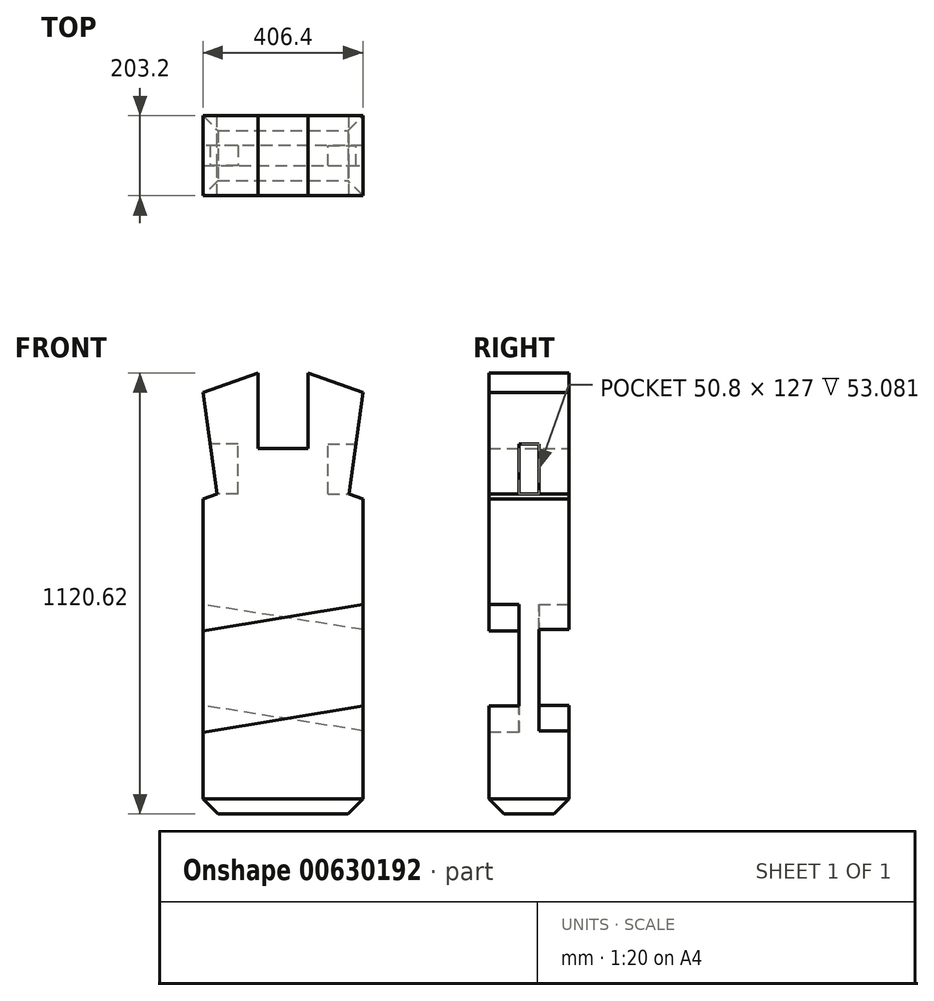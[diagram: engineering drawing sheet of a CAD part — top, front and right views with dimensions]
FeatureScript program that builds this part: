
annotation { "Feature Type Name" : "Feature", "Feature Type Description" : "" }
export const myFeature = defineFeature(function(context is Context, id is Id, definition is map)
    precondition{}
    {
        {
            var Q0;
            Q0=qCreatedBy(makeId("Front.planeOp"),FACE);
            var sketch = newSketch(context, id + "F0", { "sketchPlane" : qUnion([Q0])});
            skLineSegment(sketch, "E0.bottom", {"start": v(-203.2, 255.59) * mm, "end": v(203.2, 255.59) * mm});
            skLineSegment(sketch, "E0.top", {"start": v(-203.2, -255.59) * mm, "end": v(203.2, -255.59) * mm});
            skLineSegment(sketch, "E0.left", {"start": v(-203.2, 255.59) * mm, "end": v(-203.2, -255.59) * mm});
            skLineSegment(sketch, "E0.right", {"start": v(203.2, 255.59) * mm, "end": v(203.2, -255.59) * mm});
            skPoint(sketch, "E0.middle", {"position": v(0, 0) * mm});
            skLineSegment(sketch, "E1", {"start": v(-203.2, 255.59) * mm, "end": v(0, 329.25) * mm});
            skLineSegment(sketch, "E2", {"start": v(0, 329.25) * mm, "end": v(203.2, 255.59) * mm});
            skLineSegment(sketch, "E3", {"start": v(-167.38, -1.62) * mm, "end": v(-203.2, 255.59) * mm});
            skLineSegment(sketch, "E4", {"start": v(-167.38, -1.62) * mm, "end": v(-203.2, -14.6) * mm});
            skLineSegment(sketch, "E5", {"start": v(203.2, 255.59) * mm, "end": v(167.38, -1.62) * mm});
            skLineSegment(sketch, "E6", {"start": v(167.38, -1.62) * mm, "end": v(203.2, -14.6) * mm});
            skLineSegment(sketch, "E7.top", {"start": v(-203.2, -814.39) * mm, "end": v(203.2, -814.39) * mm});
            skLineSegment(sketch, "E7.left", {"start": v(-203.2, -255.59) * mm, "end": v(-203.2, -814.39) * mm});
            skLineSegment(sketch, "E7.right", {"start": v(203.2, -255.59) * mm, "end": v(203.2, -814.39) * mm});
            skLineSegment(sketch, "E8.bottom", {"start": v(-63.5, 349.4) * mm, "end": v(63.5, 349.4) * mm});
            skLineSegment(sketch, "E8.top", {"start": v(-63.5, 113.35) * mm, "end": v(63.5, 113.35) * mm});
            skLineSegment(sketch, "E8.left", {"start": v(-63.5, 349.4) * mm, "end": v(-63.5, 113.35) * mm});
            skLineSegment(sketch, "E8.right", {"start": v(63.5, 349.4) * mm, "end": v(63.5, 113.35) * mm});
            skPoint(sketch, "E8.middle", {"position": v(0, 231.37) * mm});
            skLineSegment(sketch, "E9.top", {"start": v(-63.5, 306.23) * mm, "end": v(63.5, 306.23) * mm});
            skLineSegment(sketch, "E9.left", {"start": v(-63.5, 349.4) * mm, "end": v(-63.5, 306.23) * mm});
            skLineSegment(sketch, "E9.right", {"start": v(63.5, 349.4) * mm, "end": v(63.5, 306.23) * mm});
            skLineSegment(sketch, "E10", {"start": v(-203.2, -255.59) * mm, "end": v(203.2, -319.01) * mm});
            skLineSegment(sketch, "E11", {"start": v(203.2, -255.59) * mm, "end": v(-203.2, -322.39) * mm});
            skLineSegment(sketch, "E12", {"start": v(-203.2, -512.66) * mm, "end": v(203.2, -576.09) * mm});
            skLineSegment(sketch, "E13", {"start": v(203.2, -513) * mm, "end": v(-203.2, -579.8) * mm});
            skSolve(sketch);
        }
        {
            var Q0;
            Q0=makeQuery(id+"F0.imprint","IMPRINT",FACE,{"disambiguationData":[TD([[makeQuery(id+"F0.imprint","IMPRINT",EDGE,{"derivedFrom":sQuery(id+"F0.wireOp",EDGE,"E0.bottom")}),-1.0]])]});
            var Q1;
            {var subQ1=sQuery(id+"F0.wireOp",EDGE,"E0.bottom");var subQ3=sQuery(id+"F0.wireOp",EDGE,"E8.left");var subQ4=makeQuery(id+"F0.imprint","INTERSECT",VERTEX,{"derivedFrom":[subQ1,subQ3]});Q1=makeQuery(id+"F0.imprint","IMPRINT",FACE,{"disambiguationData":[TD([[makeQuery(id+"F0.imprint","IMPRINT",EDGE,{"disambiguationData":[TD([[subQ4,1.0]])],"derivedFrom":subQ1}),1.0]])]});}
            var Q2;
            {var subQ1=sQuery(id+"F0.wireOp",EDGE,"E0.bottom");var subQ3=sQuery(id+"F0.wireOp",EDGE,"E8.right");var subQ4=makeQuery(id+"F0.imprint","INTERSECT",VERTEX,{"derivedFrom":[subQ1,subQ3]});Q2=makeQuery(id+"F0.imprint","IMPRINT",FACE,{"disambiguationData":[TD([[makeQuery(id+"F0.imprint","IMPRINT",EDGE,{"disambiguationData":[TD([[subQ4,-1.0]])],"derivedFrom":subQ1}),1.0]])]});}
            var Q3;
            {var subQ0=sQuery(id+"F0.wireOp",EDGE,"E0.top");Q3=makeQuery(id+"F0.imprint","IMPRINT",FACE,{"disambiguationData":[TD([[makeQuery(id+"F0.imprint","IMPRINT",EDGE,{"derivedFrom":subQ0}),-1.0]])]});}
            var Q4;
            {var subQ1=sQuery(id+"F0.wireOp",EDGE,"E7.left");var subQ3=sQuery(id+"F0.wireOp",EDGE,"E11");var subQ4=makeQuery(id+"F0.imprint","INTERSECT",VERTEX,{"derivedFrom":[subQ1,subQ3]});Q4=makeQuery(id+"F0.imprint","IMPRINT",FACE,{"disambiguationData":[TD([[makeQuery(id+"F0.imprint","IMPRINT",EDGE,{"disambiguationData":[TD([[subQ4,1.0]])],"derivedFrom":subQ3}),-1.0]])]});}
            var Q5;
            {var subQ1=sQuery(id+"F0.wireOp",EDGE,"E7.right");var subQ3=sQuery(id+"F0.wireOp",EDGE,"E10");var subQ4=makeQuery(id+"F0.imprint","INTERSECT",VERTEX,{"derivedFrom":[subQ1,subQ3]});Q5=makeQuery(id+"F0.imprint","IMPRINT",FACE,{"disambiguationData":[TD([[makeQuery(id+"F0.imprint","IMPRINT",EDGE,{"disambiguationData":[TD([[subQ4,1.0]])],"derivedFrom":subQ3}),1.0]])]});}
            var Q6;
            {var subQ3=sQuery(id+"F0.wireOp",EDGE,"E11");var subQ5=sQuery(id+"F0.wireOp",EDGE,"E7.left");var subQ6=makeQuery(id+"F0.imprint","INTERSECT",VERTEX,{"derivedFrom":[subQ5,subQ3]});Q6=makeQuery(id+"F0.imprint","IMPRINT",FACE,{"disambiguationData":[TD([[makeQuery(id+"F0.imprint","IMPRINT",EDGE,{"disambiguationData":[TD([[subQ6,-1.0]])],"derivedFrom":subQ5}),1.0]])]});}
            var Q7;
            {var subQ0=sQuery(id+"F0.wireOp",EDGE,"E12");var subQ1=sQuery(id+"F0.wireOp",EDGE,"E7.left");var subQ2=makeQuery(id+"F0.imprint","INTERSECT",VERTEX,{"derivedFrom":[subQ1,subQ0]});Q7=makeQuery(id+"F0.imprint","IMPRINT",FACE,{"disambiguationData":[TD([[makeQuery(id+"F0.imprint","IMPRINT",EDGE,{"disambiguationData":[TD([[subQ2,-1.0]])],"derivedFrom":subQ1}),1.0]])]});}
            var Q8;
            {var subQ0=sQuery(id+"F0.wireOp",EDGE,"E12");var subQ1=sQuery(id+"F0.wireOp",EDGE,"E7.right");var subQ2=makeQuery(id+"F0.imprint","INTERSECT",VERTEX,{"derivedFrom":[subQ1,subQ0]});Q8=makeQuery(id+"F0.imprint","IMPRINT",FACE,{"disambiguationData":[TD([[makeQuery(id+"F0.imprint","IMPRINT",EDGE,{"disambiguationData":[TD([[subQ2,1.0]])],"derivedFrom":subQ1}),-1.0]])]});}
            var Q9;
            {var subQ5=sQuery(id+"F0.wireOp",EDGE,"E7.top");Q9=makeQuery(id+"F0.imprint","IMPRINT",FACE,{"disambiguationData":[TD([[makeQuery(id+"F0.imprint","IMPRINT",EDGE,{"derivedFrom":subQ5}),1.0]])]});}
            extrude(context, id + "F1", {"entities" : qUnion([Q0, Q1, Q2, Q3, Q4, Q5, Q6, Q7, Q8, Q9]), "endBound" : BoundingType.SYMMETRIC, "depth" : 203.2 * mm});
        }
        {
            var Q0;
            Q0=makeQuery(id+"FCzdzIs2lLyWAf4_1.boolean.opBoolean","MERGE",FACE,{"derivedFrom":[makeQuery(id+"F1.opExtrude","SWEPT_FACE",FACE,{"disambiguationData":[OSD([sQuery(id+"F0.wireOp",EDGE,"E0.right")])]}),makeQuery(id+"FCzdzIs2lLyWAf4_1.opExtrude","SWEPT_FACE",FACE,{"disambiguationData":[OSD([sQuery(id+"F0.wireOp",EDGE,"E7.right")])]})]});
            var sketch = newSketch(context, id + "F2", { "sketchPlane" : qUnion([Q0])});
            skLineSegment(sketch, "E14.bottom", {"start": v(-25.63, -1.62) * mm, "end": v(25.17, -1.62) * mm});
            skLineSegment(sketch, "E14.top", {"start": v(-25.63, 125.38) * mm, "end": v(25.17, 125.38) * mm});
            skLineSegment(sketch, "E14.left", {"start": v(-25.63, -1.62) * mm, "end": v(-25.63, 125.38) * mm});
            skLineSegment(sketch, "E14.right", {"start": v(25.17, -1.62) * mm, "end": v(25.17, 125.38) * mm});
            skSolve(sketch);
        }
        {
            var Q0;
            Q0=makeQuery(id+"FCzdzIs2lLyWAf4_1.boolean.opBoolean","MERGE",FACE,{"derivedFrom":[makeQuery(id+"F1.opExtrude","SWEPT_FACE",FACE,{"disambiguationData":[OSD([sQuery(id+"F0.wireOp",EDGE,"E0.left")])]}),makeQuery(id+"FCzdzIs2lLyWAf4_1.opExtrude","SWEPT_FACE",FACE,{"disambiguationData":[OSD([sQuery(id+"F0.wireOp",EDGE,"E7.left")])]})]});
            var sketch = newSketch(context, id + "F3", { "sketchPlane" : qUnion([Q0])});
            skLineSegment(sketch, "E15.bottom", {"start": v(-26.2, -1.62) * mm, "end": v(25.63, -1.62) * mm});
            skLineSegment(sketch, "E15.top", {"start": v(-26.2, 125.38) * mm, "end": v(25.63, 125.38) * mm});
            skLineSegment(sketch, "E15.left", {"start": v(-26.2, -1.62) * mm, "end": v(-26.2, 125.38) * mm});
            skLineSegment(sketch, "E15.right", {"start": v(25.63, -1.62) * mm, "end": v(25.63, 125.38) * mm});
            skSolve(sketch);
        }
        {
            var Q0;
            Q0=makeQuery(id+"F3.imprint","IMPRINT",FACE,{"disambiguationData":[TD([[makeQuery(id+"F3.imprint","IMPRINT",EDGE,{"derivedFrom":sQuery(id+"F3.wireOp",EDGE,"E15.bottom")}),1.0]])]});
            extrude(context, id + "F4", {"entities" : qUnion([Q0]), "operationType" : NewBodyOperationType.REMOVE, "oppositeDirection" : true, "depth" : 88.9 * mm});
        }
        {
            var Q0;
            Q0=makeQuery(id+"F2.imprint","IMPRINT",FACE,{"disambiguationData":[TD([[makeQuery(id+"F2.imprint","IMPRINT",EDGE,{"derivedFrom":sQuery(id+"F2.wireOp",EDGE,"E14.bottom")}),1.0]])]});
            extrude(context, id + "F5", {"entities" : qUnion([Q0]), "operationType" : NewBodyOperationType.REMOVE, "oppositeDirection" : true, "depth" : 88.9 * mm});
        }
        {
            var Q0;
            Q0=makeQuery(id+"F1.opExtrude","CAP_FACE",FACE,{"disambiguationData":[OSD([sQuery(id+"F0.wireOp",EDGE,"E0.left"),sQuery(id+"F0.wireOp",EDGE,"E0.right"),sQuery(id+"F0.wireOp",EDGE,"E1"),sQuery(id+"F0.wireOp",EDGE,"E2"),sQuery(id+"F0.wireOp",EDGE,"E3"),sQuery(id+"F0.wireOp",EDGE,"E4"),sQuery(id+"F0.wireOp",EDGE,"E5"),sQuery(id+"F0.wireOp",EDGE,"E6"),sQuery(id+"F0.wireOp",EDGE,"E7.top"),sQuery(id+"F0.wireOp",EDGE,"E7.left"),sQuery(id+"F0.wireOp",EDGE,"E7.right"),sQuery(id+"F0.wireOp",EDGE,"E8.top"),sQuery(id+"F0.wireOp",EDGE,"E8.left"),sQuery(id+"F0.wireOp",EDGE,"E8.right")])],"isStart":false});
            var sketch = newSketch(context, id + "F6", { "sketchPlane" : qUnion([Q0])});
            skLineSegment(sketch, "E16", {"start": v(-203.2, -349.08) * mm, "end": v(203.2, -282.1) * mm});
            skLineSegment(sketch, "E17", {"start": v(-203.2, -606.92) * mm, "end": v(203.2, -539.95) * mm});
            skSolve(sketch);
        }
        {
            var Q0;
            {var subQ0=sQuery(id+"F6.wireOp",EDGE,"E16");Q0=makeQuery(id+"F6.imprint","IMPRINT",FACE,{"disambiguationData":[TD([[makeQuery(id+"F6.imprint","IMPRINT",EDGE,{"derivedFrom":subQ0}),-1.0]])]});}
            extrude(context, id + "F7", {"entities" : qUnion([Q0]), "operationType" : NewBodyOperationType.REMOVE, "oppositeDirection" : true, "depth" : 76.2 * mm});
        }
        {
            var Q0;
            Q0=makeQuery(id+"F1.opExtrude","CAP_FACE",FACE,{"disambiguationData":[OSD([sQuery(id+"F0.wireOp",EDGE,"E0.left"),sQuery(id+"F0.wireOp",EDGE,"E0.right"),sQuery(id+"F0.wireOp",EDGE,"E1"),sQuery(id+"F0.wireOp",EDGE,"E2"),sQuery(id+"F0.wireOp",EDGE,"E3"),sQuery(id+"F0.wireOp",EDGE,"E4"),sQuery(id+"F0.wireOp",EDGE,"E5"),sQuery(id+"F0.wireOp",EDGE,"E6"),sQuery(id+"F0.wireOp",EDGE,"E7.top"),sQuery(id+"F0.wireOp",EDGE,"E7.left"),sQuery(id+"F0.wireOp",EDGE,"E7.right"),sQuery(id+"F0.wireOp",EDGE,"E8.top"),sQuery(id+"F0.wireOp",EDGE,"E8.left"),sQuery(id+"F0.wireOp",EDGE,"E8.right")])],"isStart":true});
            var sketch = newSketch(context, id + "F8", { "sketchPlane" : qUnion([Q0])});
            skLineSegment(sketch, "E18", {"start": v(-203.2, -603.52) * mm, "end": v(203.2, -539.22) * mm});
            skLineSegment(sketch, "E19", {"start": v(-203.2, -346.33) * mm, "end": v(203.2, -282.7) * mm});
            skSolve(sketch);
        }
        {
            var Q0;
            {var subQ0=sQuery(id+"F8.wireOp",EDGE,"E18");Q0=makeQuery(id+"F8.imprint","IMPRINT",FACE,{"disambiguationData":[TD([[makeQuery(id+"F8.imprint","IMPRINT",EDGE,{"derivedFrom":subQ0}),1.0]])]});}
            extrude(context, id + "F9", {"entities" : qUnion([Q0]), "operationType" : NewBodyOperationType.REMOVE, "oppositeDirection" : true, "depth" : 76.2 * mm});
        }
        {
            var Q0;
            {var subQ0=sQuery(id+"F0.wireOp",EDGE,"E7.left");var subQ1=sQuery(id+"F0.wireOp",EDGE,"E0.left");var subQ2=sQuery(id+"F0.wireOp",EDGE,"E7.right");var subQ3=sQuery(id+"F0.wireOp",EDGE,"E0.right");var subQ4=sQuery(id+"F0.wireOp",EDGE,"E7.top");Q0=makeQuery(id+"F7.boolean.opBoolean","SPLIT",FACE,{"disambiguationData":[TD([makeQuery(id+"F1.opExtrude","SWEPT_FACE",FACE,{"disambiguationData":[OSD([subQ4])]})])],"derivedFrom":makeQuery(id+"F1.opExtrude","CAP_FACE",FACE,{"disambiguationData":[OSD([subQ1,subQ3,sQuery(id+"F0.wireOp",EDGE,"E1"),sQuery(id+"F0.wireOp",EDGE,"E2"),sQuery(id+"F0.wireOp",EDGE,"E3"),sQuery(id+"F0.wireOp",EDGE,"E4"),sQuery(id+"F0.wireOp",EDGE,"E5"),sQuery(id+"F0.wireOp",EDGE,"E6"),subQ4,subQ0,subQ2,sQuery(id+"F0.wireOp",EDGE,"E8.top"),sQuery(id+"F0.wireOp",EDGE,"E8.left"),sQuery(id+"F0.wireOp",EDGE,"E8.right")])],"isStart":false})});}
            var sketch = newSketch(context, id + "F10", { "sketchPlane" : qUnion([Q0])});
            skLineSegment(sketch, "E20", {"start": v(165.1, -814.39) * mm, "end": v(203.2, -776.29) * mm});
            skLineSegment(sketch, "E21", {"start": v(-203.2, -776.29) * mm, "end": v(-165.1, -814.39) * mm});
            skSolve(sketch);
        }
        {
            var Q0;
            {var subQ0=sQuery(id+"F10.wireOp",EDGE,"E20");Q0=makeQuery(id+"F10.imprint","IMPRINT",FACE,{"disambiguationData":[TD([[makeQuery(id+"F10.imprint","IMPRINT",EDGE,{"derivedFrom":subQ0}),-1.0]])]});}
            var Q1;
            {var subQ0=sQuery(id+"F10.wireOp",EDGE,"E21");Q1=makeQuery(id+"F10.imprint","IMPRINT",FACE,{"disambiguationData":[TD([[makeQuery(id+"F10.imprint","IMPRINT",EDGE,{"derivedFrom":subQ0}),-1.0]])]});}
            extrude(context, id + "F11", {"entities" : qUnion([Q0, Q1]), "operationType" : NewBodyOperationType.REMOVE, "oppositeDirection" : true, "depth" : 203.2 * mm, "offsetDistance" : 25.4 * mm});
        }
        {
            var Q0;
            Q0=makeQuery(id+"F1.opExtrude","SWEPT_FACE",FACE,{"disambiguationData":[OSD([sQuery(id+"F0.wireOp",EDGE,"E0.right"),sQuery(id+"F0.wireOp",EDGE,"E7.right")])]});
            var sketch = newSketch(context, id + "F12", { "sketchPlane" : qUnion([Q0])});
            skLineSegment(sketch, "E22", {"start": v(-101.6, -776.29) * mm, "end": v(-63.5, -814.39) * mm});
            skLineSegment(sketch, "E23", {"start": v(-63.5, -814.39) * mm, "end": v(-101.6, -814.39) * mm});
            skLineSegment(sketch, "E24", {"start": v(-101.6, -814.39) * mm, "end": v(-101.6, -776.29) * mm});
            skLineSegment(sketch, "E25", {"start": v(101.6, -776.29) * mm, "end": v(101.6, -814.39) * mm});
            skLineSegment(sketch, "E26", {"start": v(101.6, -814.39) * mm, "end": v(63.5, -814.39) * mm});
            skLineSegment(sketch, "E27", {"start": v(63.5, -814.39) * mm, "end": v(101.6, -776.29) * mm});
            skSolve(sketch);
        }
        {
            var Q0;
            Q0=makeQuery(id+"F12.imprint","IMPRINT",FACE,{"disambiguationData":[TD([[makeQuery(id+"F12.imprint","IMPRINT",EDGE,{"derivedFrom":sQuery(id+"F12.wireOp",EDGE,"E22")}),-1.0]])]});
            var Q1;
            Q1=makeQuery(id+"F12.imprint","IMPRINT",FACE,{"disambiguationData":[TD([[makeQuery(id+"F12.imprint","IMPRINT",EDGE,{"derivedFrom":sQuery(id+"F12.wireOp",EDGE,"E25")}),-1.0]])]});
            extrude(context, id + "F13", {"entities" : qUnion([Q0, Q1]), "operationType" : NewBodyOperationType.REMOVE, "oppositeDirection" : true, "depth" : 406.4 * mm, "offsetDistance" : 25.4 * mm});
        }
    });
